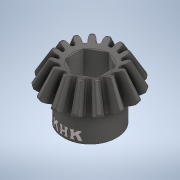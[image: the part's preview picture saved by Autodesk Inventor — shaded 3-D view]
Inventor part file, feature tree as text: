
AUTODESK INVENTOR PART (.ipt)
format: ipt  version: 2020 (Build 240168000, 168)  size: 1,448,960 bytes
history: native  units: in
note: dims shown in document units (in); Inventor stores cm internally (conversion verified against a paired STEP export)
features: extrude x1, sketch x1, imported_body x1
ambient origin geometry x8: Origin, YZ Plane, XZ Plane, XY Plane, X Axis, Y Axis, Z Axis, Center Point
bodies: Solid1 (feature_tree)
feature tree (3):
  extrude  "Extrusion1"  Depth=0.375in TaperAngle=0.0deg
  sketch  "Sketch1"  dims[d0=0.375in d1=0.3937in d2=0.0in]
  imported_body  "Base1"
